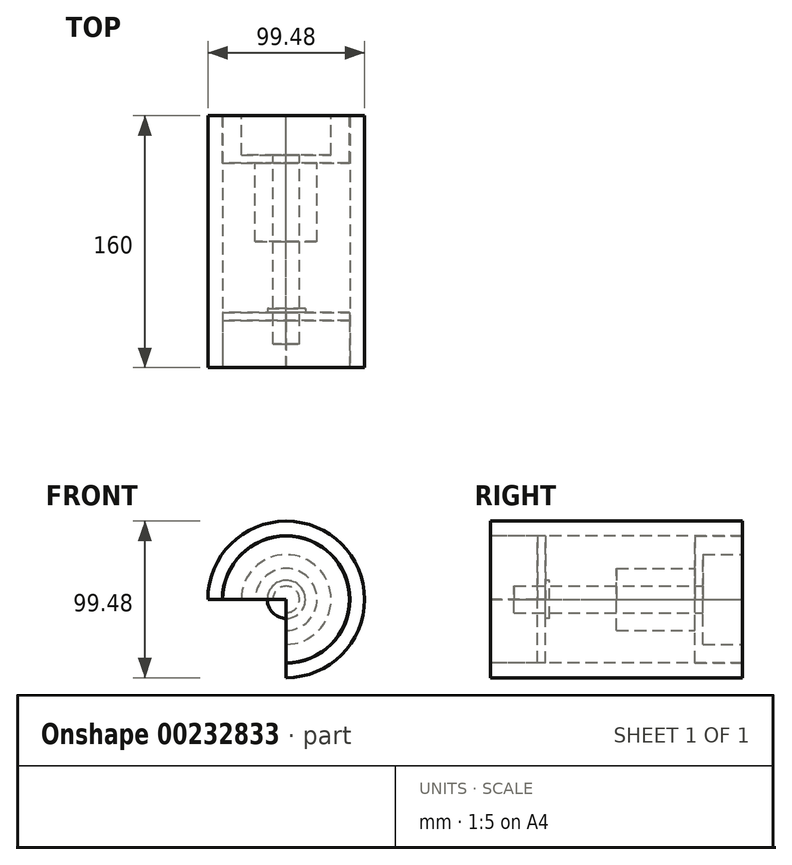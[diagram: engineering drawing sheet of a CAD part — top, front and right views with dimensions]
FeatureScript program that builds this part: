
annotation { "Feature Type Name" : "Feature", "Feature Type Description" : "" }
export const myFeature = defineFeature(function(context is Context, id is Id, definition is map)
    precondition{}
    {
        {
            var Q0;
            Q0=qCreatedBy(makeId("Front.planeOp"),FACE);
            var sketch = newSketch(context, id + "F0", { "sketchPlane" : qUnion([Q0])});
            skCircle(sketch, "E0", {"center": v(0, 0) * mm, "radius": 49.74 * mm});
            skSolve(sketch);
        }
        {
            var Q0;
            Q0 = qSketchRegion(id + "F0", true);
            extrude(context, id + "F1", {"entities" : qUnion([Q0]), "endBound" : BoundingType.SYMMETRIC, "depth" : 160 * mm});
        }
        {
            var Q0;
            Q0=qCreatedBy(makeId("Front.planeOp"),FACE);
            var sketch = newSketch(context, id + "F2", { "sketchPlane" : qUnion([Q0])});
            skCircle(sketch, "E1", {"center": v(0, 0) * mm, "radius": 40.46 * mm});
            skSolve(sketch);
        }
        {
            var Q0;
            Q0 = qSketchRegion(id + "F2", true);
            extrude(context, id + "F3", {"entities" : qUnion([Q0]), "operationType" : NewBodyOperationType.REMOVE, "endBound" : BoundingType.SYMMETRIC, "oppositeDirection" : true, "depth" : 180 * mm});
        }
        {
            var Q0;
            Q0=qCreatedBy(makeId("Front.planeOp"),FACE);
            var sketch = newSketch(context, id + "F4", { "sketchPlane" : qUnion([Q0])});
            skCircle(sketch, "E2", {"center": v(0, 0) * mm, "radius": 8.45 * mm});
            skSolve(sketch);
        }
        {
            var Q0;
            Q0 = qSketchRegion(id + "F4", true);
            extrude(context, id + "F5", {"entities" : qUnion([Q0]), "endBound" : BoundingType.SYMMETRIC, "depth" : 130 * mm});
        }
        {
            var Q0;
            Q0=qCreatedBy(makeId("Front.planeOp"),FACE);
            cPlane(context, id + "F6", {"entities" : qUnion([Q0]), "cplaneType" : CPlaneType.OFFSET, "offset" : 80 * mm, "width" : 150 * mm, "height" : 150 * mm});
        }
        {
            var Q0;
            Q0=qCreatedBy(id+"F6.planeOp",FACE);
            var sketch = newSketch(context, id + "F7", { "sketchPlane" : qUnion([Q0])});
            skCircle(sketch, "E3", {"center": v(0, 0) * mm, "radius": 40.25 * mm});
            skSolve(sketch);
        }
        {
            var Q0;
            Q0 = qSketchRegion(id + "F7", true);
            extrude(context, id + "F8", {"entities" : qUnion([Q0]), "oppositeDirection" : true, "depth" : 30 * mm});
        }
        {
            var Q0;
            Q0=qCreatedBy(id+"F6.planeOp",FACE);
            cPlane(context, id + "F9", {"entities" : qUnion([Q0]), "cplaneType" : CPlaneType.OFFSET, "offset" : 30 * mm, "oppositeDirection" : true, "width" : 150 * mm, "height" : 150 * mm});
        }
        {
            var Q0;
            Q0=qCreatedBy(id+"F9.planeOp",FACE);
            var sketch = newSketch(context, id + "F10", { "sketchPlane" : qUnion([Q0])});
            skCircle(sketch, "E4", {"center": v(0, 0) * mm, "radius": 40.35 * mm});
            skSolve(sketch);
        }
        {
            var Q0;
            Q0 = qSketchRegion(id + "F10", true);
            extrude(context, id + "F11", {"entities" : qUnion([Q0]), "oppositeDirection" : true, "depth" : 5 * mm});
        }
        {
            var Q0;
            Q0=qCreatedBy(makeId("Front.planeOp"),FACE);
            cPlane(context, id + "F12", {"entities" : qUnion([Q0]), "cplaneType" : CPlaneType.OFFSET, "offset" : 80 * mm, "oppositeDirection" : true, "width" : 150 * mm, "height" : 150 * mm});
        }
        {
            var Q0;
            Q0=qCreatedBy(id+"F12.planeOp",FACE);
            var sketch = newSketch(context, id + "F13", { "sketchPlane" : qUnion([Q0])});
            skCircle(sketch, "E5", {"center": v(0, 0) * mm, "radius": 40.25 * mm});
            skSolve(sketch);
        }
        {
            var Q0;
            Q0 = qSketchRegion(id + "F13", true);
            extrude(context, id + "F14", {"entities" : qUnion([Q0]), "depth" : 30 * mm});
        }
        {
            var Q0;
            Q0=qCreatedBy(id+"F12.planeOp",FACE);
            cPlane(context, id + "F15", {"entities" : qUnion([Q0]), "cplaneType" : CPlaneType.OFFSET, "offset" : 30 * mm, "width" : 150 * mm, "height" : 150 * mm});
        }
        {
            var Q0;
            Q0=qCreatedBy(id+"F15.planeOp",FACE);
            var sketch = newSketch(context, id + "F16", { "sketchPlane" : qUnion([Q0])});
            skCircle(sketch, "E6", {"center": v(0, 0) * mm, "radius": 19.63 * mm});
            skSolve(sketch);
        }
        {
            var Q0;
            Q0 = qSketchRegion(id + "F16", true);
            extrude(context, id + "F17", {"entities" : qUnion([Q0]), "depth" : 50 * mm});
        }
        {
            var Q0;
            Q0=qCreatedBy(id+"F12.planeOp",FACE);
            var sketch = newSketch(context, id + "F18", { "sketchPlane" : qUnion([Q0])});
            skCircle(sketch, "E7", {"center": v(0, 0) * mm, "radius": 28.5 * mm});
            skSolve(sketch);
        }
        {
            var Q0;
            Q0 = qSketchRegion(id + "F18", true);
            extrude(context, id + "F19", {"entities" : qUnion([Q0]), "operationType" : NewBodyOperationType.REMOVE, "depth" : 25 * mm});
        }
        {
            var Q0;
            Q0=qCreatedBy(id+"F12.planeOp",FACE);
            var sketch = newSketch(context, id + "F20", { "sketchPlane" : qUnion([Q0])});
            skLineSegment(sketch, "E8.bottom", {"start": v(0, 0) * mm, "end": v(-76.7, 0) * mm});
            skLineSegment(sketch, "E8.top", {"start": v(0, -61.77) * mm, "end": v(-76.7, -61.77) * mm});
            skLineSegment(sketch, "E8.left", {"start": v(0, 0) * mm, "end": v(0, -61.77) * mm});
            skLineSegment(sketch, "E8.right", {"start": v(-76.7, 0) * mm, "end": v(-76.7, -61.77) * mm});
            skSolve(sketch);
        }
        {
            var Q0;
            Q0 = qSketchRegion(id + "F20", true);
            extrude(context, id + "F21", {"entities" : qUnion([Q0]), "operationType" : NewBodyOperationType.REMOVE, "depth" : 180 * mm});
        }
        {
            var Q0;
            Q0=qCreatedBy(makeId("Front.planeOp"),FACE);
            cPlane(context, id + "F22", {"entities" : qUnion([Q0]), "cplaneType" : CPlaneType.OFFSET, "offset" : 45 * mm, "width" : 150 * mm, "height" : 150 * mm});
        }
        {
            var Q0;
            Q0=qCreatedBy(id+"F22.planeOp",FACE);
            var sketch = newSketch(context, id + "F23", { "sketchPlane" : qUnion([Q0])});
            skCircle(sketch, "E9", {"center": v(0.1, 0.03) * mm, "radius": 12.07 * mm});
            skSolve(sketch);
        }
        {
            var Q0;
            Q0 = qSketchRegion(id + "F23", true);
            extrude(context, id + "F24", {"entities" : qUnion([Q0]), "oppositeDirection" : true, "depth" : 2.5 * mm});
        }
    });
